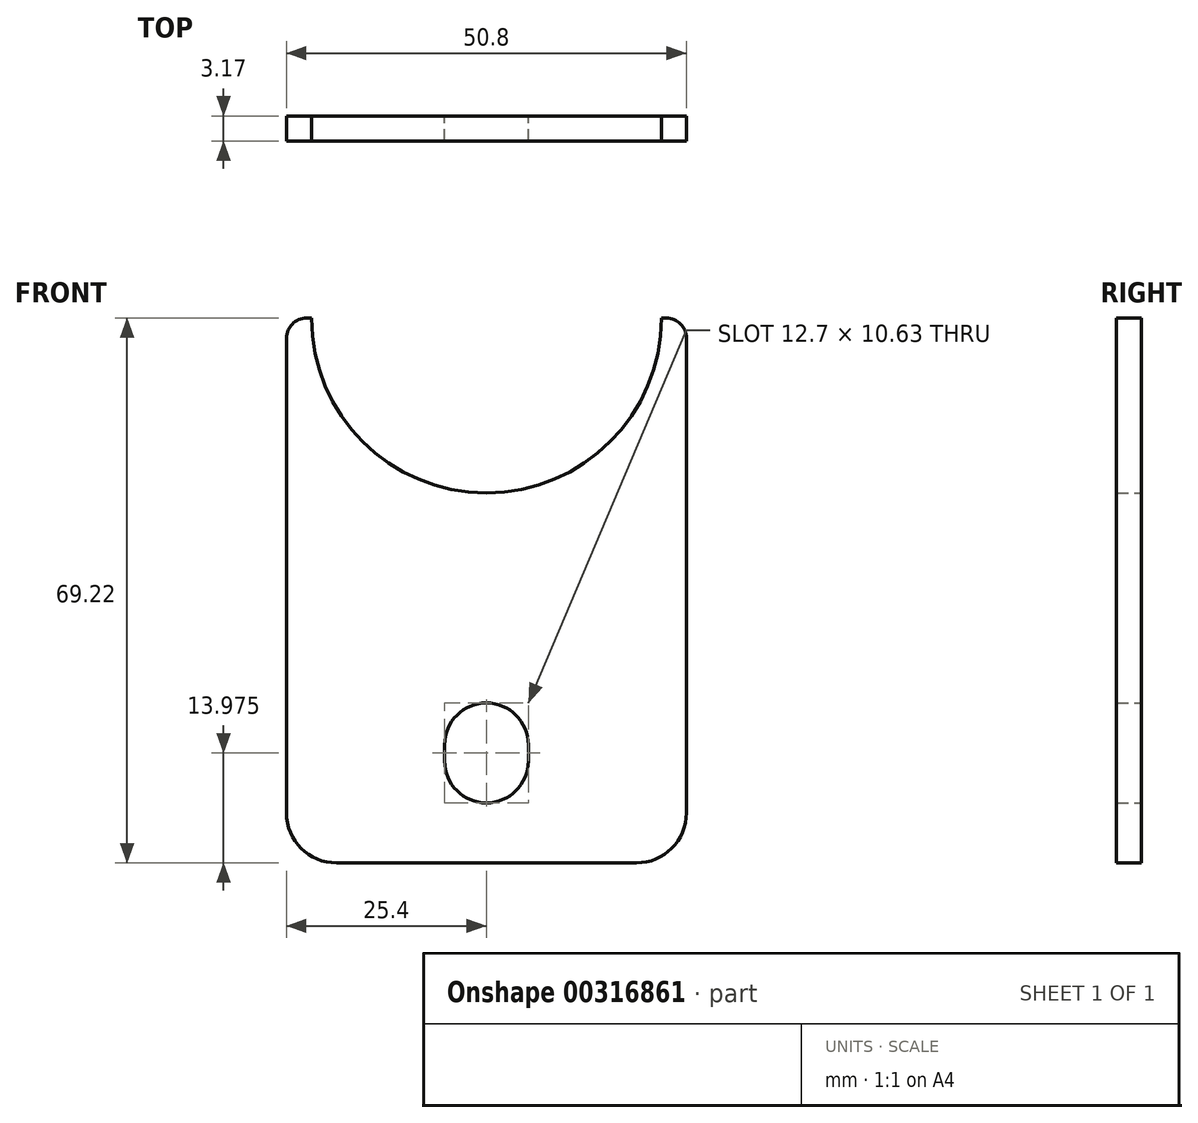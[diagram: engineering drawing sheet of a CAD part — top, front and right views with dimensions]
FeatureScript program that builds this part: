
annotation { "Feature Type Name" : "Feature", "Feature Type Description" : "" }
export const myFeature = defineFeature(function(context is Context, id is Id, definition is map)
    precondition{}
    {
        {
            var Q0;
            Q0=qCreatedBy(makeId("Front.planeOp"),FACE);
            var sketch = newSketch(context, id + "F0", { "sketchPlane" : qUnion([Q0])});
            skArc(sketch, "E0", {"start": v(-22.23, 0) * mm, "mid": v(0, -22.23) * mm, "end": v(22.23, 0) * mm});
            skArc(sketch, "E1", {"start": v(5.31, -54.2) * mm, "mid": v(0, -48.9) * mm, "end": v(-5.31, -54.2) * mm});
            skArc(sketch, "E2", {"start": v(-5.31, -56.28) * mm, "mid": v(0, -61.6) * mm, "end": v(5.31, -56.28) * mm});
            skLineSegment(sketch, "E3", {"start": v(-5.31, -54.2) * mm, "end": v(-5.31, -56.28) * mm});
            skLineSegment(sketch, "E4", {"start": v(5.31, -54.2) * mm, "end": v(5.31, -56.28) * mm});
            skLineSegment(sketch, "E5", {"start": v(0, -69.22) * mm, "end": v(19.05, -69.22) * mm});
            skLineSegment(sketch, "E6", {"start": v(0, -69.22) * mm, "end": v(-19.05, -69.22) * mm});
            skLineSegment(sketch, "E7", {"start": v(-25.4, -62.87) * mm, "end": v(-25.4, -2.54) * mm});
            skLineSegment(sketch, "E8", {"start": v(25.4, -62.87) * mm, "end": v(25.4, -2.54) * mm});
            skLineSegment(sketch, "E9", {"start": v(-22.86, 0) * mm, "end": v(-22.23, 0) * mm});
            skLineSegment(sketch, "E10", {"start": v(22.86, 0) * mm, "end": v(22.23, 0) * mm});
            skPoint(sketch, "E11.end.orphan", {"position": v(5.31, -55.25) * mm});
            skPoint(sketch, "E11.start.orphan", {"position": v(-5.31, -55.25) * mm});
            skPoint(sketch, "E12.visualSharp", {"position": v(-25.4, -69.22) * mm});
            skArc(sketch, "E12.filletArc", {"start": v(-25.4, -62.87) * mm, "mid": v(-23.54, -67.36) * mm, "end": v(-19.05, -69.22) * mm});
            skPoint(sketch, "E13.visualSharp", {"position": v(25.4, -69.22) * mm});
            skArc(sketch, "E13.filletArc", {"start": v(19.05, -69.22) * mm, "mid": v(23.54, -67.36) * mm, "end": v(25.4, -62.87) * mm});
            skPoint(sketch, "E14.visualSharp", {"position": v(-25.4, 0) * mm});
            skArc(sketch, "E14.filletArc", {"start": v(-22.86, 0) * mm, "mid": v(-24.66, -0.74) * mm, "end": v(-25.4, -2.54) * mm});
            skPoint(sketch, "E15.visualSharp", {"position": v(25.4, 0) * mm});
            skArc(sketch, "E15.filletArc", {"start": v(25.4, -2.54) * mm, "mid": v(24.66, -0.74) * mm, "end": v(22.86, 0) * mm});
            skSolve(sketch);
        }
        {
            var Q0;
            Q0 = qSketchRegion(id + "F0", true);
            extrude(context, id + "F1", {"entities" : qUnion([Q0]), "depth" : 3.17 * mm});
        }
    });
